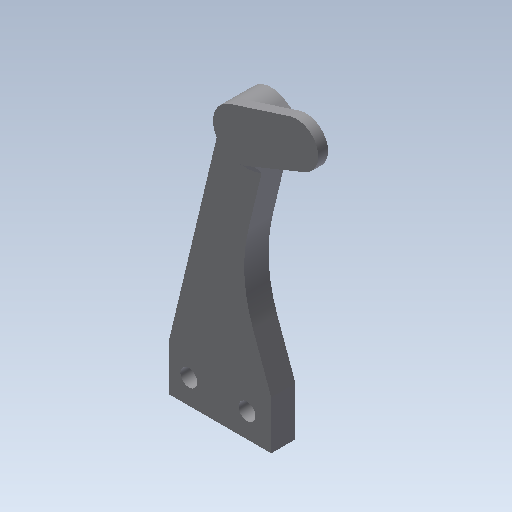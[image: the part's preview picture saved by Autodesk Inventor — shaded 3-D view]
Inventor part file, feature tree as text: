
AUTODESK INVENTOR PART (.ipt)
format: ipt  version: 2020.1 (Build 241239000, 239)  size: 137,728 bytes
history: native  units: mm
features: extrude x2, sketch x2, chamfer x1
ambient origin geometry x8: Origin, YZ Plane, XZ Plane, XY Plane, X Axis, Y Axis, Z Axis, Center Point
bodies: Solid1 (feature_tree)
feature tree (5):
  extrude  "Extrusion1"  Depth=6.0mm
  extrude  "Extrusion2"  Depth=10.0mm
  chamfer  "Chamfer2"  Distance=5.0mm
  sketch  "Sketch1"  dims[d0=6.0mm d1=12.0mm]
  sketch  "Sketch2"  dims[d2=3.5mm d3=3.5mm d4=5.0mm d5=11.0mm d6=10.0mm d7=10.0mm d8=10.0mm d9=20.0mm d10=19.198622mm d11=30.0mm d12=10.0mm d13=19.198622mm d14=30.0mm d15=2.0mm d16=5.0mm d17=5.0mm d18=0.0mm d22=2.0mm d23=0.0mm d27=13.0mm d28=3.490659mm d29=9.0mm d30=2.0mm d31=2.0mm d32=45.0deg]
